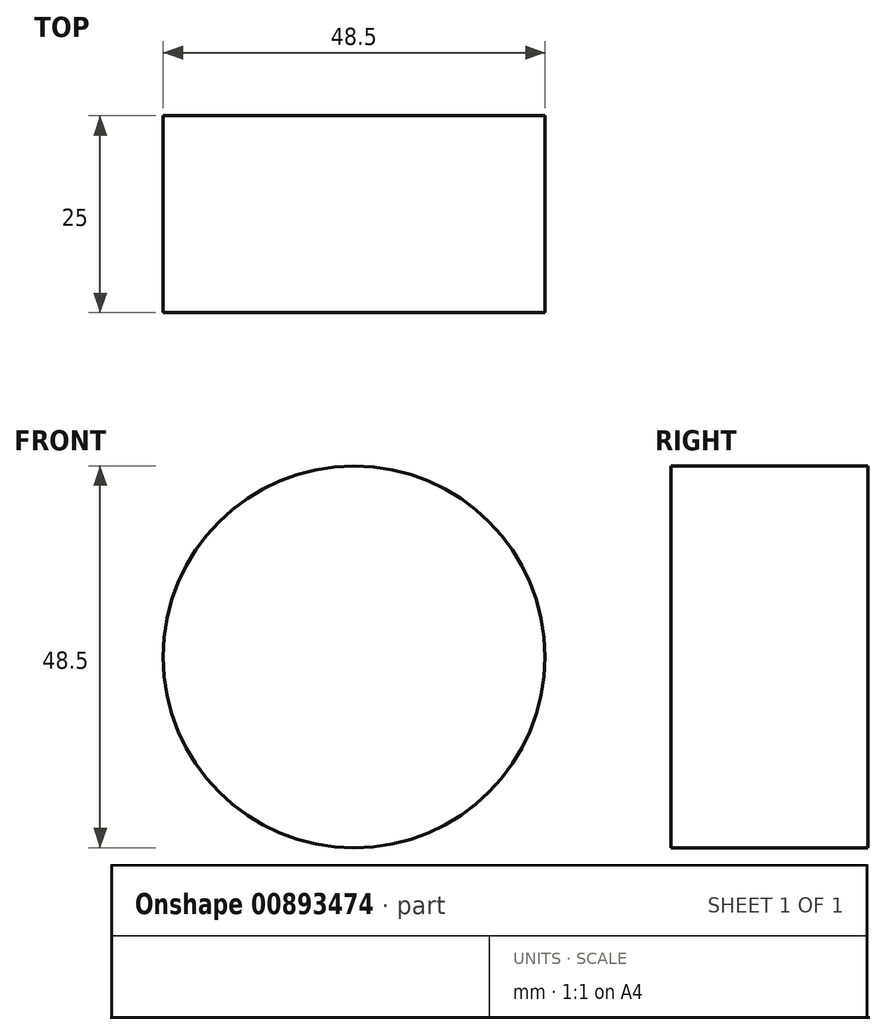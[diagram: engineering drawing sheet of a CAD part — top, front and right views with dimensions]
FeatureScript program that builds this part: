
annotation { "Feature Type Name" : "Feature", "Feature Type Description" : "" }
export const myFeature = defineFeature(function(context is Context, id is Id, definition is map)
    precondition{}
    {
        {
            var Q0;
            Q0=qCreatedBy(makeId("Front.planeOp"),FACE);
            var sketch = newSketch(context, id + "F0", { "sketchPlane" : qUnion([Q0])});
            skCircle(sketch, "E0", {"center": v(0, 0) * mm, "radius": 24.25 * mm});
            skSolve(sketch);
        }
        {
            var Q0;
            Q0=makeQuery(id+"F0.imprint","IMPRINT",FACE,{"disambiguationData":[TD([[makeQuery(id+"F0.imprint","IMPRINT",EDGE,{"derivedFrom":sQuery(id+"F0.wireOp",EDGE,"E0")}),1.0]])]});
            extrude(context, id + "F1", {"entities" : qUnion([Q0]), "depth" : 25 * mm, "offsetDistance" : 25 * mm});
        }
    });
